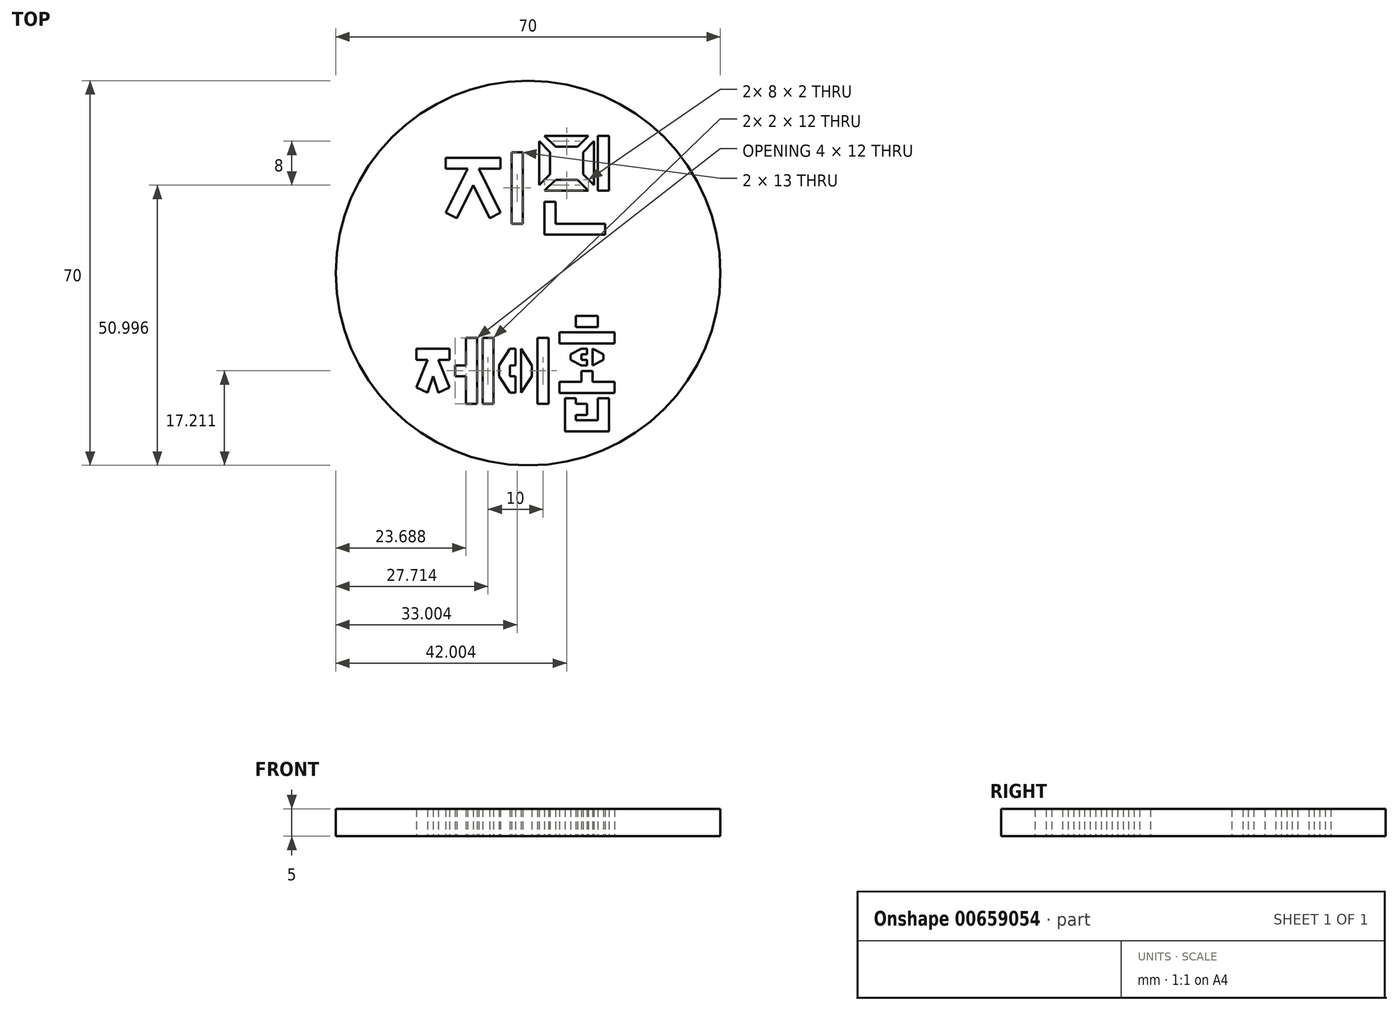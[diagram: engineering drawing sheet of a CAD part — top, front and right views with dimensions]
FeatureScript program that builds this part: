
annotation { "Feature Type Name" : "Feature", "Feature Type Description" : "" }
export const myFeature = defineFeature(function(context is Context, id is Id, definition is map)
    precondition{}
    {
        {
            var Q0;
            Q0=qCreatedBy(makeId("Top.planeOp"),FACE);
            var sketch = newSketch(context, id + "F0", { "sketchPlane" : qUnion([Q0])});
            skLineSegment(sketch, "E0.bottom", {"start": v(-48.95, 54.58) * mm, "end": v(-38.95, 54.58) * mm});
            skLineSegment(sketch, "E0.left", {"start": v(-48.95, 54.58) * mm, "end": v(-48.95, 52.58) * mm});
            skLineSegment(sketch, "E0.right", {"start": v(-38.95, 54.58) * mm, "end": v(-38.95, 52.58) * mm});
            skLineSegment(sketch, "E1.top", {"start": v(-48.95, 52.58) * mm, "end": v(-44.95, 52.58) * mm});
            skLineSegment(sketch, "E2.bottom", {"start": v(-42.95, 52.58) * mm, "end": v(-38.95, 52.58) * mm});
            skLineSegment(sketch, "E3", {"start": v(-44.95, 52.58) * mm, "end": v(-48.95, 44.58) * mm});
            skLineSegment(sketch, "E4", {"start": v(-42.95, 52.58) * mm, "end": v(-38.95, 44.58) * mm});
            skLineSegment(sketch, "E5", {"start": v(-48.95, 44.58) * mm, "end": v(-46.95, 43.58) * mm});
            skLineSegment(sketch, "E6", {"start": v(-38.95, 44.58) * mm, "end": v(-40.95, 43.58) * mm});
            skLineSegment(sketch, "E7", {"start": v(-36.95, 55.58) * mm, "end": v(-34.95, 55.58) * mm});
            skLineSegment(sketch, "E8", {"start": v(-36.95, 42.58) * mm, "end": v(-34.95, 42.58) * mm});
            skLineSegment(sketch, "E9", {"start": v(-34.95, 55.58) * mm, "end": v(-34.95, 42.58) * mm});
            skLineSegment(sketch, "E10", {"start": v(-36.95, 55.58) * mm, "end": v(-36.95, 42.58) * mm});
            skLineSegment(sketch, "E11.bottom", {"start": v(-30.95, 58.58) * mm, "end": v(-22.95, 58.58) * mm});
            skLineSegment(sketch, "E11.top", {"start": v(-30.95, 48.58) * mm, "end": v(-22.95, 48.58) * mm});
            skLineSegment(sketch, "E11.left", {"start": v(-31.95, 57.58) * mm, "end": v(-31.95, 49.58) * mm});
            skLineSegment(sketch, "E11.right", {"start": v(-21.95, 57.58) * mm, "end": v(-21.95, 49.58) * mm});
            skLineSegment(sketch, "E12", {"start": v(-28.96, 56.58) * mm, "end": v(-24.96, 56.58) * mm});
            skLineSegment(sketch, "E13", {"start": v(-29.96, 55.58) * mm, "end": v(-29.96, 51.58) * mm});
            skLineSegment(sketch, "E14", {"start": v(-23.96, 55.58) * mm, "end": v(-23.96, 51.58) * mm});
            skLineSegment(sketch, "E15", {"start": v(-28.96, 50.58) * mm, "end": v(-24.96, 50.58) * mm});
            skLineSegment(sketch, "E16", {"start": v(-30.95, 58.58) * mm, "end": v(-28.96, 56.58) * mm});
            skLineSegment(sketch, "E17", {"start": v(-31.95, 57.58) * mm, "end": v(-29.96, 55.58) * mm});
            skLineSegment(sketch, "E18", {"start": v(-31.95, 49.58) * mm, "end": v(-29.96, 51.58) * mm});
            skLineSegment(sketch, "E19", {"start": v(-24.96, 50.58) * mm, "end": v(-22.95, 48.58) * mm});
            skLineSegment(sketch, "E20", {"start": v(-23.96, 51.58) * mm, "end": v(-21.95, 49.58) * mm});
            skLineSegment(sketch, "E21", {"start": v(-24.96, 56.58) * mm, "end": v(-22.95, 58.58) * mm});
            skLineSegment(sketch, "E22", {"start": v(-21.95, 57.58) * mm, "end": v(-23.96, 55.58) * mm});
            skLineSegment(sketch, "E23", {"start": v(-28.96, 50.58) * mm, "end": v(-30.95, 48.58) * mm});
            skLineSegment(sketch, "E24", {"start": v(-21.24, 58.58) * mm, "end": v(-19.24, 58.58) * mm});
            skLineSegment(sketch, "E25.bottom", {"start": v(-19.24, 58.58) * mm, "end": v(-21.24, 58.58) * mm});
            skLineSegment(sketch, "E25.top", {"start": v(-19.24, 48.58) * mm, "end": v(-21.24, 48.58) * mm});
            skLineSegment(sketch, "E25.left", {"start": v(-19.24, 58.58) * mm, "end": v(-19.24, 48.58) * mm});
            skLineSegment(sketch, "E25.right", {"start": v(-21.24, 58.58) * mm, "end": v(-21.24, 48.58) * mm});
            skLineSegment(sketch, "E26.bottom", {"start": v(-30.95, 46.58) * mm, "end": v(-28.95, 46.58) * mm});
            skLineSegment(sketch, "E26.top", {"start": v(-30.95, 40.58) * mm, "end": v(-28.95, 40.58) * mm});
            skLineSegment(sketch, "E26.left", {"start": v(-30.95, 46.58) * mm, "end": v(-30.95, 40.58) * mm});
            skLineSegment(sketch, "E26.right", {"start": v(-28.95, 46.58) * mm, "end": v(-28.95, 42.58) * mm});
            skLineSegment(sketch, "E27.bottom", {"start": v(-28.95, 40.58) * mm, "end": v(-19.95, 40.58) * mm});
            skLineSegment(sketch, "E27.top", {"start": v(-28.95, 42.58) * mm, "end": v(-19.95, 42.58) * mm});
            skLineSegment(sketch, "E27.right", {"start": v(-19.95, 40.58) * mm, "end": v(-19.95, 42.58) * mm});
            skLineSegment(sketch, "E28", {"start": v(-18.24, 22.8) * mm, "end": v(-18.24, 20.8) * mm});
            skLineSegment(sketch, "E29.bottom", {"start": v(-25.24, 25.78) * mm, "end": v(-21.24, 25.78) * mm});
            skLineSegment(sketch, "E29.top", {"start": v(-25.24, 23.78) * mm, "end": v(-21.24, 23.78) * mm});
            skLineSegment(sketch, "E29.left", {"start": v(-25.24, 25.78) * mm, "end": v(-25.24, 23.78) * mm});
            skLineSegment(sketch, "E29.right", {"start": v(-21.24, 25.78) * mm, "end": v(-21.24, 23.78) * mm});
            skLineSegment(sketch, "E30", {"start": v(-28.24, 22.8) * mm, "end": v(-28.24, 20.8) * mm});
            skLineSegment(sketch, "E31", {"start": v(-28.24, 20.8) * mm, "end": v(-18.24, 20.8) * mm});
            skLineSegment(sketch, "E32", {"start": v(-27.24, 10.78) * mm, "end": v(-25.24, 10.78) * mm});
            skLineSegment(sketch, "E33", {"start": v(-27.24, 10.78) * mm, "end": v(-26.24, 10.78) * mm});
            skLineSegment(sketch, "E34", {"start": v(-19.24, 10.78) * mm, "end": v(-20.24, 10.78) * mm});
            skLineSegment(sketch, "E35", {"start": v(-25.24, 6.78) * mm, "end": v(-21.24, 6.78) * mm});
            skLineSegment(sketch, "E36", {"start": v(-27.24, 10.78) * mm, "end": v(-27.24, 4.78) * mm});
            skLineSegment(sketch, "E37", {"start": v(-19.24, 10.78) * mm, "end": v(-19.24, 4.78) * mm});
            skLineSegment(sketch, "E38", {"start": v(-20.24, 10.78) * mm, "end": v(-21.24, 10.78) * mm});
            skLineSegment(sketch, "E39", {"start": v(-26.24, 10.78) * mm, "end": v(-25.24, 10.78) * mm});
            skLineSegment(sketch, "E40", {"start": v(-21.24, 10.78) * mm, "end": v(-21.24, 6.78) * mm});
            skLineSegment(sketch, "E41", {"start": v(-25.24, 6.78) * mm, "end": v(-25.24, 7.78) * mm});
            skLineSegment(sketch, "E42", {"start": v(-25.24, 10.78) * mm, "end": v(-25.24, 9.78) * mm});
            skLineSegment(sketch, "E43", {"start": v(-25.24, 9.78) * mm, "end": v(-23.24, 9.78) * mm});
            skLineSegment(sketch, "E44", {"start": v(-23.24, 9.78) * mm, "end": v(-23.24, 7.78) * mm});
            skLineSegment(sketch, "E45", {"start": v(-23.24, 7.78) * mm, "end": v(-25.24, 7.78) * mm});
            skLineSegment(sketch, "E46", {"start": v(-27.24, 4.78) * mm, "end": v(-19.24, 4.78) * mm});
            skLineSegment(sketch, "E47", {"start": v(-28.24, 11.78) * mm, "end": v(-28.24, 13.78) * mm});
            skLineSegment(sketch, "E48", {"start": v(-28.24, 13.78) * mm, "end": v(-18.24, 13.78) * mm});
            skLineSegment(sketch, "E49", {"start": v(-28.24, 11.78) * mm, "end": v(-18.24, 11.78) * mm});
            skLineSegment(sketch, "E50", {"start": v(-28.24, 13.78) * mm, "end": v(-24.24, 13.78) * mm});
            skLineSegment(sketch, "E51", {"start": v(-18.24, 13.78) * mm, "end": v(-22.24, 13.78) * mm});
            skLineSegment(sketch, "E52", {"start": v(-24.24, 13.78) * mm, "end": v(-24.24, 15.78) * mm});
            skLineSegment(sketch, "E53", {"start": v(-24.24, 15.78) * mm, "end": v(-22.24, 15.78) * mm});
            skLineSegment(sketch, "E54", {"start": v(-22.24, 15.78) * mm, "end": v(-22.24, 13.78) * mm});
            skLineSegment(sketch, "E55.trimOffspring", {"start": v(-21.24, 10.78) * mm, "end": v(-19.24, 10.78) * mm});
            skLineSegment(sketch, "E56.trimOffspring", {"start": v(-18.24, 13.78) * mm, "end": v(-18.24, 11.78) * mm});
            skLineSegment(sketch, "E57.top", {"start": v(-24.24, 16.8) * mm, "end": v(-23.24, 16.8) * mm});
            skLineSegment(sketch, "E57.left", {"start": v(-26.24, 18.8) * mm, "end": v(-26.24, 17.8) * mm});
            skLineSegment(sketch, "E57.right", {"start": v(-20.24, 18.8) * mm, "end": v(-20.24, 17.8) * mm});
            skLineSegment(sketch, "E58", {"start": v(-24.24, 19.8) * mm, "end": v(-23.24, 19.8) * mm});
            skLineSegment(sketch, "E59", {"start": v(-23.24, 19.8) * mm, "end": v(-23.24, 18.8) * mm});
            skLineSegment(sketch, "E60", {"start": v(-22.24, 19.8) * mm, "end": v(-22.24, 16.8) * mm});
            skLineSegment(sketch, "E61", {"start": v(-22.24, 19.8) * mm, "end": v(-20.24, 18.8) * mm});
            skLineSegment(sketch, "E62", {"start": v(-20.24, 17.8) * mm, "end": v(-22.24, 16.8) * mm});
            skLineSegment(sketch, "E63", {"start": v(-24.24, 19.8) * mm, "end": v(-26.24, 18.8) * mm});
            skLineSegment(sketch, "E64", {"start": v(-26.24, 17.8) * mm, "end": v(-24.24, 16.8) * mm});
            skLineSegment(sketch, "E65", {"start": v(-23.24, 18.8) * mm, "end": v(-24.24, 18.8) * mm});
            skLineSegment(sketch, "E66", {"start": v(-24.24, 18.8) * mm, "end": v(-24.24, 17.8) * mm});
            skLineSegment(sketch, "E67", {"start": v(-24.24, 17.8) * mm, "end": v(-23.24, 17.8) * mm});
            skLineSegment(sketch, "E68.trimOffspring", {"start": v(-23.24, 17.8) * mm, "end": v(-23.24, 16.8) * mm});
            skLineSegment(sketch, "E69.trimOffspring", {"start": v(-28.24, 13.78) * mm, "end": v(-28.24, 11.78) * mm});
            skLineSegment(sketch, "E70", {"start": v(-28.24, 22.8) * mm, "end": v(-28.24, 21.8) * mm});
            skLineSegment(sketch, "E71", {"start": v(-28.24, 22.8) * mm, "end": v(-18.24, 22.8) * mm});
            skLineSegment(sketch, "E72", {"start": v(-30.24, 21.8) * mm, "end": v(-32.24, 21.8) * mm});
            skLineSegment(sketch, "E73", {"start": v(-32.24, 21.8) * mm, "end": v(-30.24, 21.8) * mm});
            skLineSegment(sketch, "E74", {"start": v(-30.24, 21.8) * mm, "end": v(-30.24, 9.8) * mm});
            skLineSegment(sketch, "E75", {"start": v(-30.24, 9.8) * mm, "end": v(-32.24, 9.8) * mm});
            skLineSegment(sketch, "E76", {"start": v(-32.24, 21.8) * mm, "end": v(-32.24, 9.8) * mm});
            skLineSegment(sketch, "E77", {"start": v(-32.24, 21.8) * mm, "end": v(-32.24, 19.8) * mm});
            skLineSegment(sketch, "E78", {"start": v(-32.24, 9.8) * mm, "end": v(-32.24, 11.8) * mm});
            skLineSegment(sketch, "E79", {"start": v(-39.24, 16.8) * mm, "end": v(-39.24, 14.8) * mm});
            skLineSegment(sketch, "E80", {"start": v(-37.24, 11.8) * mm, "end": v(-36.24, 11.8) * mm});
            skLineSegment(sketch, "E81", {"start": v(-37.24, 19.8) * mm, "end": v(-39.24, 16.8) * mm});
            skLineSegment(sketch, "E82", {"start": v(-35.24, 19.8) * mm, "end": v(-33.24, 16.8) * mm});
            skLineSegment(sketch, "E83", {"start": v(-39.24, 14.8) * mm, "end": v(-37.24, 11.8) * mm});
            skLineSegment(sketch, "E84", {"start": v(-33.24, 14.8) * mm, "end": v(-35.24, 11.8) * mm});
            skLineSegment(sketch, "E85", {"start": v(-37.24, 19.8) * mm, "end": v(-36.24, 19.8) * mm});
            skLineSegment(sketch, "E86", {"start": v(-36.24, 14.8) * mm, "end": v(-36.24, 11.8) * mm});
            skLineSegment(sketch, "E87", {"start": v(-35.24, 19.8) * mm, "end": v(-35.24, 11.8) * mm});
            skLineSegment(sketch, "E88", {"start": v(-37.24, 16.8) * mm, "end": v(-36.24, 16.8) * mm});
            skLineSegment(sketch, "E89", {"start": v(-37.24, 16.8) * mm, "end": v(-37.24, 14.8) * mm});
            skLineSegment(sketch, "E90", {"start": v(-37.24, 14.8) * mm, "end": v(-36.24, 14.8) * mm});
            skLineSegment(sketch, "E91", {"start": v(-36.24, 19.8) * mm, "end": v(-36.24, 16.8) * mm});
            skLineSegment(sketch, "E92", {"start": v(-33.24, 16.8) * mm, "end": v(-33.24, 14.8) * mm});
            skLineSegment(sketch, "E93", {"start": v(-40.24, 21.8) * mm, "end": v(-42.26, 21.8) * mm});
            skLineSegment(sketch, "E94", {"start": v(-42.26, 21.8) * mm, "end": v(-41.26, 21.8) * mm});
            skLineSegment(sketch, "E95.bottom", {"start": v(-40.24, 21.8) * mm, "end": v(-42.24, 21.8) * mm});
            skLineSegment(sketch, "E95.top", {"start": v(-40.24, 9.8) * mm, "end": v(-42.24, 9.8) * mm});
            skLineSegment(sketch, "E95.left", {"start": v(-40.24, 21.8) * mm, "end": v(-40.24, 9.8) * mm});
            skLineSegment(sketch, "E95.right", {"start": v(-42.24, 21.8) * mm, "end": v(-42.24, 9.8) * mm});
            skLineSegment(sketch, "E96.left", {"start": v(-43.26, 21.8) * mm, "end": v(-43.26, 9.8) * mm});
            skLineSegment(sketch, "E97", {"start": v(-43.26, 21.8) * mm, "end": v(-45.26, 21.8) * mm});
            skLineSegment(sketch, "E98", {"start": v(-45.26, 9.8) * mm, "end": v(-43.26, 9.8) * mm});
            skLineSegment(sketch, "E99", {"start": v(-45.26, 21.8) * mm, "end": v(-45.26, 16.8) * mm});
            skLineSegment(sketch, "E100", {"start": v(-45.26, 9.8) * mm, "end": v(-45.26, 14.8) * mm});
            skLineSegment(sketch, "E101", {"start": v(-45.26, 16.8) * mm, "end": v(-47.26, 16.8) * mm});
            skLineSegment(sketch, "E102", {"start": v(-47.26, 16.8) * mm, "end": v(-47.26, 14.8) * mm});
            skLineSegment(sketch, "E103", {"start": v(-47.26, 14.8) * mm, "end": v(-45.26, 14.8) * mm});
            skLineSegment(sketch, "E104.trimOffspring", {"start": v(-45.26, 14.8) * mm, "end": v(-45.26, 9.8) * mm});
            skLineSegment(sketch, "E105.bottom", {"start": v(-48.26, 19.8) * mm, "end": v(-54.26, 19.8) * mm});
            skLineSegment(sketch, "E105.left", {"start": v(-48.26, 19.8) * mm, "end": v(-48.26, 17.8) * mm});
            skLineSegment(sketch, "E105.right", {"start": v(-54.26, 19.8) * mm, "end": v(-54.26, 17.8) * mm});
            skLineSegment(sketch, "E106", {"start": v(-54.26, 17.8) * mm, "end": v(-48.26, 17.8) * mm});
            skLineSegment(sketch, "E107", {"start": v(-54.26, 17.8) * mm, "end": v(-52.26, 17.8) * mm});
            skLineSegment(sketch, "E108", {"start": v(-52.26, 17.8) * mm, "end": v(-50.26, 17.8) * mm});
            skLineSegment(sketch, "E109", {"start": v(-54.26, 12.8) * mm, "end": v(-52.26, 11.8) * mm});
            skLineSegment(sketch, "E110", {"start": v(-50.26, 11.8) * mm, "end": v(-48.26, 12.8) * mm});
            skLineSegment(sketch, "E111", {"start": v(-48.26, 12.8) * mm, "end": v(-50.26, 17.8) * mm});
            skLineSegment(sketch, "E112", {"start": v(-52.26, 17.8) * mm, "end": v(-54.26, 12.8) * mm});
            skLineSegment(sketch, "E113", {"start": v(-51.26, 14.8) * mm, "end": v(-50.26, 11.8) * mm});
            skLineSegment(sketch, "E114", {"start": v(-51.26, 14.8) * mm, "end": v(-52.26, 11.8) * mm});
            skCircle(sketch, "E115", {"center": v(-33.95, 33.58) * mm, "radius": 35 * mm});
            skLineSegment(sketch, "E116", {"start": v(-43.95, 49.58) * mm, "end": v(-46.95, 43.58) * mm});
            skLineSegment(sketch, "E117", {"start": v(-43.95, 49.58) * mm, "end": v(-40.95, 43.58) * mm});
            skSolve(sketch);
        }
        {
            var Q0;
            Q0=makeQuery(id+"F0.imprint","IMPRINT",FACE,{"disambiguationData":[TD([[makeQuery(id+"F0.imprint","IMPRINT",EDGE,{"derivedFrom":sQuery(id+"F0.wireOp",EDGE,"E0.bottom")}),1.0]])]});
            extrude(context, id + "F1", {"entities" : qUnion([Q0]), "depth" : 5 * mm, "offsetDistance" : 25 * mm});
        }
    });
